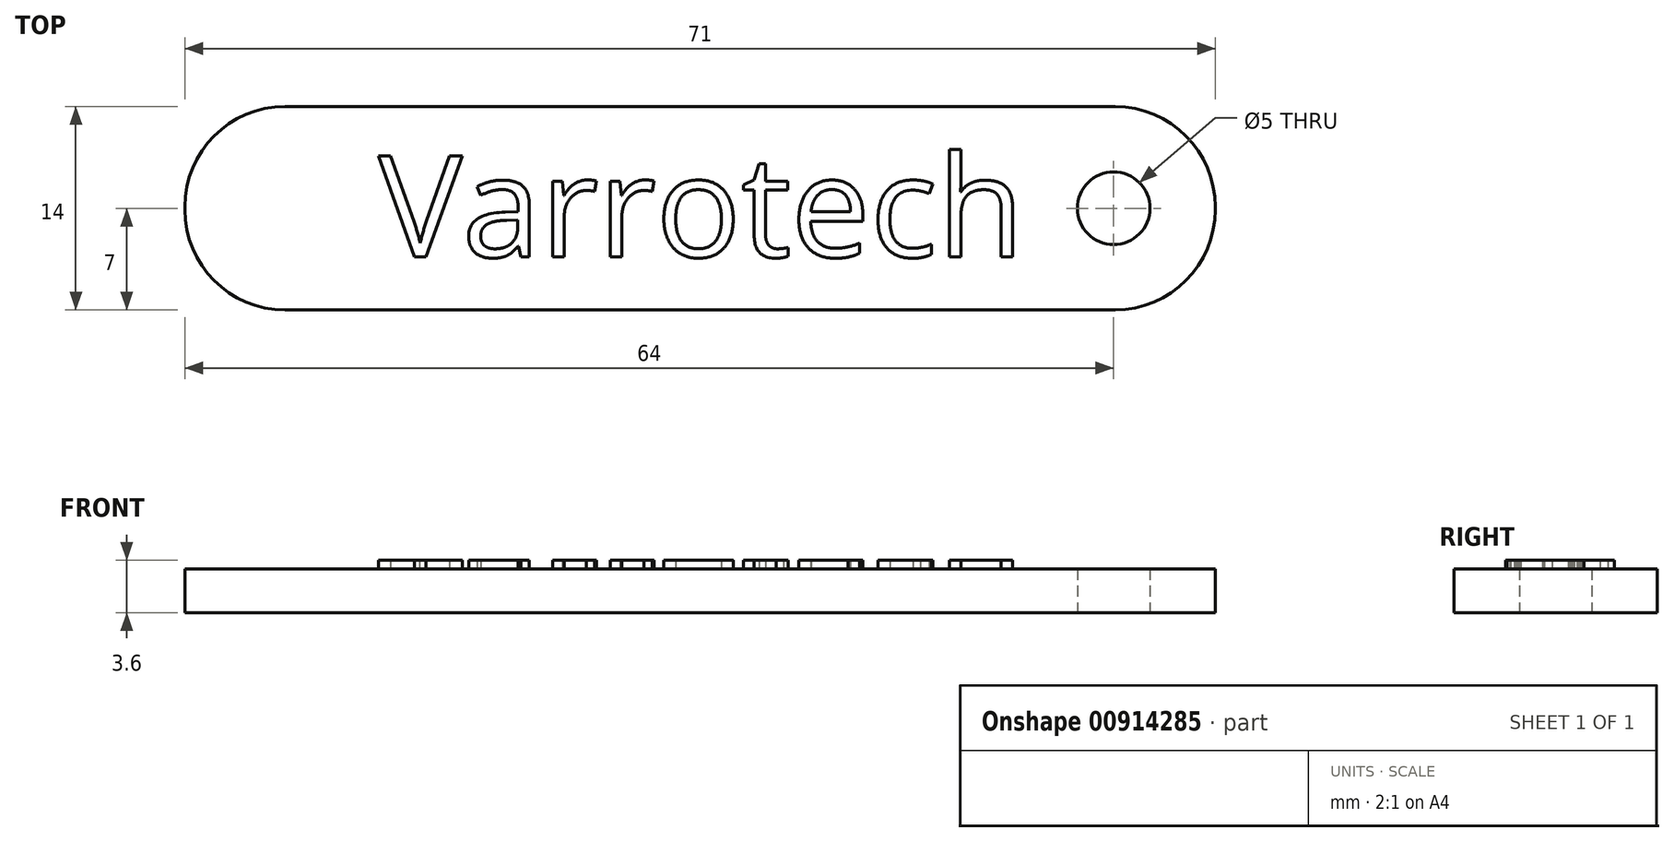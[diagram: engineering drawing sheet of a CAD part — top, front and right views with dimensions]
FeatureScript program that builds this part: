
annotation { "Feature Type Name" : "Feature", "Feature Type Description" : "" }
export const myFeature = defineFeature(function(context is Context, id is Id, definition is map)
    precondition{}
    {
        {
            var Q0;
            Q0=qCreatedBy(makeId("Top.planeOp"),FACE);
            var sketch = newSketch(context, id + "F0", { "sketchPlane" : qUnion([Q0])});
            skLineSegment(sketch, "E0.bottom", {"start": v(35.5, -7) * mm, "end": v(-35.5, -7) * mm});
            skLineSegment(sketch, "E0.top", {"start": v(35.5, 7) * mm, "end": v(-35.5, 7) * mm});
            skLineSegment(sketch, "E0.left", {"start": v(35.5, -7) * mm, "end": v(35.5, 7) * mm});
            skLineSegment(sketch, "E0.right", {"start": v(-35.5, -7) * mm, "end": v(-35.5, 7) * mm});
            skPoint(sketch, "E0.middle", {"position": v(0, 0) * mm});
            skCircle(sketch, "E1", {"center": v(28.5, 0) * mm, "radius": 2.5 * mm});
            skSolve(sketch);
        }
        {
            var Q0;
            Q0=makeQuery(id+"F0.imprint","IMPRINT",FACE,{"disambiguationData":[TD([[makeQuery(id+"F0.imprint","IMPRINT",EDGE,{"derivedFrom":sQuery(id+"F0.wireOp",EDGE,"E0.bottom")}),-1.0]])]});
            extrude(context, id + "F1", {"entities" : qUnion([Q0]), "depth" : 3 * mm, "offsetDistance" : 25 * mm});
        }
        {
            var Q0;
            Q0=makeQuery(id+"F1.opExtrude","SWEPT_EDGE",EDGE,{"disambiguationData":[OSD([sQuery(id+"F0.wireOp",EDGE,"E0.bottom"),sQuery(id+"F0.wireOp",EDGE,"E0.left")])]});
            var Q1;
            Q1=makeQuery(id+"F1.opExtrude","SWEPT_EDGE",EDGE,{"disambiguationData":[OSD([sQuery(id+"F0.wireOp",EDGE,"E0.top"),sQuery(id+"F0.wireOp",EDGE,"E0.left")])]});
            var Q2;
            Q2=makeQuery(id+"F1.opExtrude","SWEPT_EDGE",EDGE,{"disambiguationData":[OSD([sQuery(id+"F0.wireOp",EDGE,"E0.bottom"),sQuery(id+"F0.wireOp",EDGE,"E0.right")])]});
            var Q3;
            Q3=makeQuery(id+"F1.opExtrude","SWEPT_EDGE",EDGE,{"disambiguationData":[OSD([sQuery(id+"F0.wireOp",EDGE,"E0.top"),sQuery(id+"F0.wireOp",EDGE,"E0.right")])]});
            fillet(context, id + "F2", {"entities" : qUnion([Q0, Q1, Q2, Q3]), "radius" : 6.9 * mm, "tangentPropagation" : true, "allowEdgeOverflow" : false});
        }
        {
            var Q0;
            Q0=makeQuery(id+"F1.opExtrude","CAP_FACE",FACE,{"disambiguationData":[OSD([sQuery(id+"F0.wireOp",EDGE,"E0.bottom"),sQuery(id+"F0.wireOp",EDGE,"E0.top"),sQuery(id+"F0.wireOp",EDGE,"E0.left"),sQuery(id+"F0.wireOp",EDGE,"E0.right"),sQuery(id+"F0.wireOp",EDGE,"E1")])],"isStart":false});
            var sketch = newSketch(context, id + "F3", { "sketchPlane" : qUnion([Q0])});
            skText(sketch, "E2", { "text": "Varrotech", "fontName": "OpenSans-Regular.ttf"});
            const initialGuessF3  = {"E2": [-0.02217, -0.00335, 1, 0, 0.007]};
            skSetInitialGuess(sketch, initialGuessF3);
            skSolve(sketch);
        }
        {
            var Q0;
            Q0 = qSketchRegion(id + "F3", true);
            extrude(context, id + "F4", {"entities" : qUnion([Q0]), "operationType" : NewBodyOperationType.ADD, "depth" : 0.6 * mm, "offsetDistance" : 25 * mm});
        }
    });
